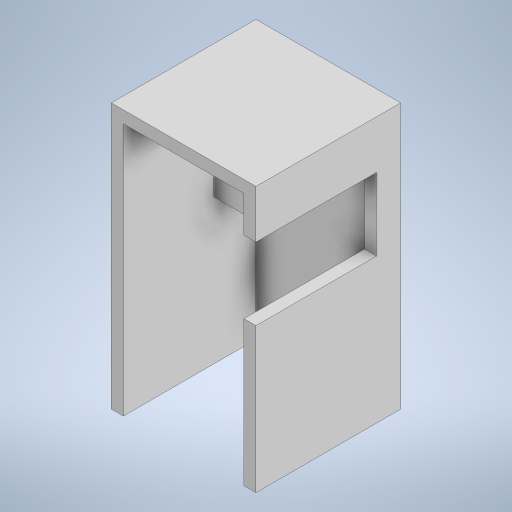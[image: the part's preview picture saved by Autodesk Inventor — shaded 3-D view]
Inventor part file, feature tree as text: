
AUTODESK INVENTOR PART (.ipt)
format: ipt  version: 2023 (Build 270158000, 158)  size: 225,280 bytes
history: native  units: in
note: dims shown in document units (in); Inventor stores cm internally (conversion verified against a paired STEP export)
features: sketch x4, extrude x4
ambient origin geometry x8: Origin, YZ Plane, XZ Plane, XY Plane, X Axis, Y Axis, Z Axis, Center Point
bodies: Solid1 (feature_tree)
feature tree (8):
  sketch  "Sketch1"  dims[d0=0.4724in d1=0.4724in]
  sketch  "Sketch2"  dims[d2=0.3937in d3=0.7874in]
  extrude  "Extrusion1"  Depth=0.4724in
  extrude  "Extrusion2"  Depth=0.3937in
  extrude  "Extrusion3"  Depth=0.8268in TaperAngle=0.0deg
  extrude  "Extrusion4"  Depth=0.0394in TaperAngle=0.0deg
  sketch  "Sketch3"  dims[d4=0.8661in d5=0.0in d6=0.8268in d7=0.0in]
  sketch  "Sketch4"  dims[d8=0.2362in d9=0.0394in d10=0.0in d11=0.1772in d12=0.1378in d13=0.3543in d14=0.0in]
